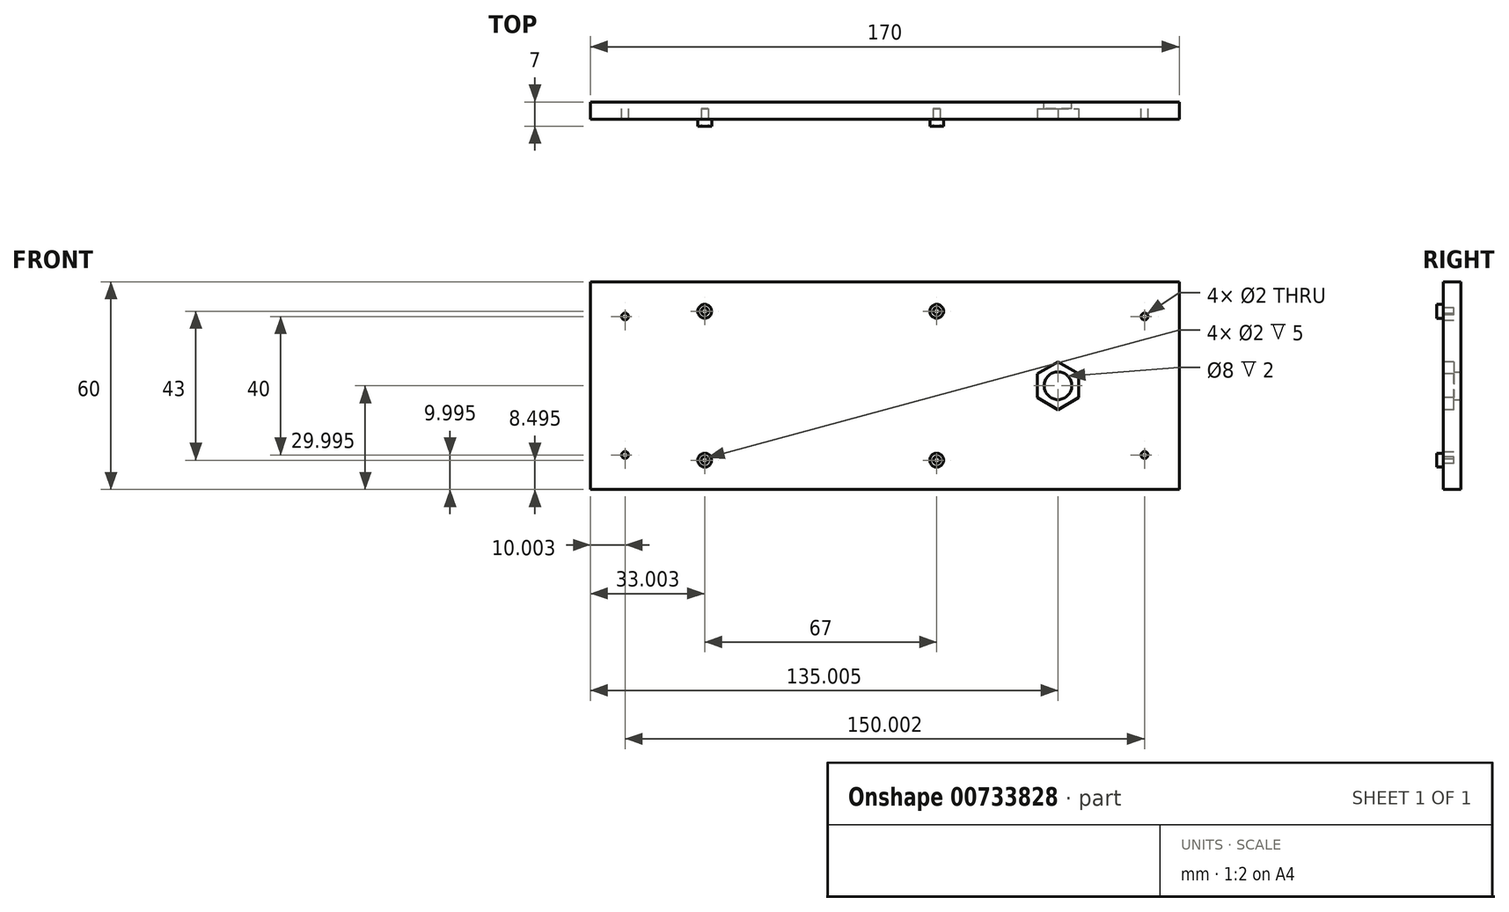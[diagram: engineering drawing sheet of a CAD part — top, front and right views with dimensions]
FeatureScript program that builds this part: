
annotation { "Feature Type Name" : "Feature", "Feature Type Description" : "" }
export const myFeature = defineFeature(function(context is Context, id is Id, definition is map)
    precondition{}
    {
        {
            var Q0;
            Q0=qCreatedBy(makeId("Front.planeOp"),FACE);
            var sketch = newSketch(context, id + "F0", { "sketchPlane" : qUnion([Q0])});
            skLineSegment(sketch, "E0.1", {"start": v(-75.65, -37.91) * mm, "end": v(-75.65, 22.09) * mm});
            skCircle(sketch, "E1", {"center": v(-65.65, -27.91) * mm, "radius": 1 * mm});
            skCircle(sketch, "E2", {"center": v(-65.65, 12.09) * mm, "radius": 1 * mm});
            skLineSegment(sketch, "E3.MirrorCS", {"start": v(94.35, 22.09) * mm, "end": v(-75.65, 22.09) * mm});
            skLineSegment(sketch, "E4.MirrorCS", {"start": v(94.35, -37.91) * mm, "end": v(94.35, 22.09) * mm});
            skCircle(sketch, "E5.MirrorC", {"center": v(84.35, 12.09) * mm, "radius": 1 * mm});
            skCircle(sketch, "E6.MirrorC", {"center": v(84.35, -27.91) * mm, "radius": 1 * mm});
            skLineSegment(sketch, "E7", {"start": v(-75.65, -37.91) * mm, "end": v(94.35, -37.91) * mm});
            skLineSegment(sketch, "E8", {"start": v(-75.65, 22.09) * mm, "end": v(-75.65, -7.91) * mm});
            skLineSegment(sketch, "E9", {"start": v(94.35, 22.09) * mm, "end": v(59.35, 22.09) * mm});
            skCircle(sketch, "E10", {"center": v(59.35, -7.91) * mm, "radius": 4 * mm});
            skLineSegment(sketch, "E11", {"start": v(-75.65, 22.09) * mm, "end": v(24.35, 22.09) * mm});
            skCircle(sketch, "E12", {"center": v(-42.65, -29.41) * mm, "radius": 2 * mm});
            skCircle(sketch, "E13", {"center": v(24.35, -29.41) * mm, "radius": 2 * mm});
            skCircle(sketch, "E14", {"center": v(24.35, 13.59) * mm, "radius": 2 * mm});
            skCircle(sketch, "E15", {"center": v(-42.65, 13.59) * mm, "radius": 2 * mm});
            skCircle(sketch, "E16", {"center": v(-42.65, 13.59) * mm, "radius": 1 * mm});
            skCircle(sketch, "E17", {"center": v(24.35, 13.59) * mm, "radius": 1 * mm});
            skCircle(sketch, "E18", {"center": v(24.35, -29.41) * mm, "radius": 1 * mm});
            skCircle(sketch, "E19", {"center": v(-42.65, -29.41) * mm, "radius": 1 * mm});
            skLineSegment(sketch, "E20.0", {"start": v(65.35, -4.45) * mm, "end": v(65.35, -11.38) * mm});
            skLineSegment(sketch, "E20.1", {"start": v(65.35, -11.38) * mm, "end": v(59.35, -14.84) * mm});
            skLineSegment(sketch, "E20.2", {"start": v(59.35, -14.84) * mm, "end": v(53.35, -11.38) * mm});
            skLineSegment(sketch, "E20.3", {"start": v(53.35, -11.38) * mm, "end": v(53.35, -4.45) * mm});
            skLineSegment(sketch, "E20.4", {"start": v(53.35, -4.45) * mm, "end": v(59.35, -0.99) * mm});
            skLineSegment(sketch, "E20.5", {"start": v(59.35, -0.99) * mm, "end": v(65.35, -4.45) * mm});
            skPoint(sketch, "E20.0.midPoint", {"position": v(65.35, -7.91) * mm});
            skSolve(sketch);
        }
        {
            var Q0;
            Q0=makeQuery(id+"F0.imprint","IMPRINT",FACE,{"disambiguationData":[TD([[makeQuery(id+"F0.imprint","IMPRINT",EDGE,{"derivedFrom":sQuery(id+"F0.wireOp",EDGE,"E18")}),1.0]])]});
            var Q1;
            Q1=makeQuery(id+"F0.imprint","IMPRINT",FACE,{"disambiguationData":[TD([[makeQuery(id+"F0.imprint","IMPRINT",EDGE,{"derivedFrom":sQuery(id+"F0.wireOp",EDGE,"E13")}),1.0]])]});
            var Q2;
            Q2=makeQuery(id+"F0.imprint","IMPRINT",FACE,{"disambiguationData":[TD([[makeQuery(id+"F0.imprint","IMPRINT",EDGE,{"derivedFrom":sQuery(id+"F0.wireOp",EDGE,"E0.1")}),-1.0]])]});
            var Q3;
            Q3=makeQuery(id+"F0.imprint","IMPRINT",FACE,{"disambiguationData":[TD([[makeQuery(id+"F0.imprint","IMPRINT",EDGE,{"derivedFrom":sQuery(id+"F0.wireOp",EDGE,"E12")}),1.0]])]});
            var Q4;
            Q4=makeQuery(id+"F0.imprint","IMPRINT",FACE,{"disambiguationData":[TD([[makeQuery(id+"F0.imprint","IMPRINT",EDGE,{"derivedFrom":sQuery(id+"F0.wireOp",EDGE,"E19")}),1.0]])]});
            var Q5;
            Q5=makeQuery(id+"F0.imprint","IMPRINT",FACE,{"disambiguationData":[TD([[makeQuery(id+"F0.imprint","IMPRINT",EDGE,{"derivedFrom":sQuery(id+"F0.wireOp",EDGE,"E15")}),1.0]])]});
            var Q6;
            Q6=makeQuery(id+"F0.imprint","IMPRINT",FACE,{"disambiguationData":[TD([[makeQuery(id+"F0.imprint","IMPRINT",EDGE,{"derivedFrom":sQuery(id+"F0.wireOp",EDGE,"E16")}),1.0]])]});
            var Q7;
            Q7=makeQuery(id+"F0.imprint","IMPRINT",FACE,{"disambiguationData":[TD([[makeQuery(id+"F0.imprint","IMPRINT",EDGE,{"derivedFrom":sQuery(id+"F0.wireOp",EDGE,"E14")}),1.0]])]});
            var Q8;
            Q8=makeQuery(id+"F0.imprint","IMPRINT",FACE,{"disambiguationData":[TD([[makeQuery(id+"F0.imprint","IMPRINT",EDGE,{"derivedFrom":sQuery(id+"F0.wireOp",EDGE,"E17")}),1.0]])]});
            var Q9;
            Q9=makeQuery(id+"F0.imprint","IMPRINT",FACE,{"disambiguationData":[TD([[makeQuery(id+"F0.imprint","IMPRINT",EDGE,{"derivedFrom":sQuery(id+"F0.wireOp",EDGE,"E10")}),-1.0]])]});
            extrude(context, id + "F1", {"entities" : qUnion([Q0, Q1, Q2, Q3, Q4, Q5, Q6, Q7, Q8, Q9]), "depth" : 5 * mm, "offsetDistance" : 25.4 * mm});
        }
        {
            var Q0;
            Q0=makeQuery(id+"F0.imprint","IMPRINT",FACE,{"disambiguationData":[TD([[makeQuery(id+"F0.imprint","IMPRINT",EDGE,{"derivedFrom":sQuery(id+"F0.wireOp",EDGE,"E19")}),1.0]])]});
            var Q1;
            Q1=makeQuery(id+"F0.imprint","IMPRINT",FACE,{"disambiguationData":[TD([[makeQuery(id+"F0.imprint","IMPRINT",EDGE,{"derivedFrom":sQuery(id+"F0.wireOp",EDGE,"E16")}),1.0]])]});
            var Q2;
            Q2=makeQuery(id+"F0.imprint","IMPRINT",FACE,{"disambiguationData":[TD([[makeQuery(id+"F0.imprint","IMPRINT",EDGE,{"derivedFrom":sQuery(id+"F0.wireOp",EDGE,"E17")}),1.0]])]});
            var Q3;
            Q3=makeQuery(id+"F0.imprint","IMPRINT",FACE,{"disambiguationData":[TD([[makeQuery(id+"F0.imprint","IMPRINT",EDGE,{"derivedFrom":sQuery(id+"F0.wireOp",EDGE,"E18")}),1.0]])]});
            var Q4;
            Q4=makeQuery(id+"F0.imprint","IMPRINT",FACE,{"disambiguationData":[TD([[makeQuery(id+"F0.imprint","IMPRINT",EDGE,{"derivedFrom":sQuery(id+"F0.wireOp",EDGE,"E15")}),1.0]])]});
            var Q5;
            Q5=makeQuery(id+"F0.imprint","IMPRINT",FACE,{"disambiguationData":[TD([[makeQuery(id+"F0.imprint","IMPRINT",EDGE,{"derivedFrom":sQuery(id+"F0.wireOp",EDGE,"E12")}),1.0]])]});
            var Q6;
            Q6=makeQuery(id+"F0.imprint","IMPRINT",FACE,{"disambiguationData":[TD([[makeQuery(id+"F0.imprint","IMPRINT",EDGE,{"derivedFrom":sQuery(id+"F0.wireOp",EDGE,"E13")}),1.0]])]});
            var Q7;
            Q7=makeQuery(id+"F0.imprint","IMPRINT",FACE,{"disambiguationData":[TD([[makeQuery(id+"F0.imprint","IMPRINT",EDGE,{"derivedFrom":sQuery(id+"F0.wireOp",EDGE,"E14")}),1.0]])]});
            extrude(context, id + "F2", {"entities" : qUnion([Q0, Q1, Q2, Q3, Q4, Q5, Q6, Q7]), "operationType" : NewBodyOperationType.ADD, "depth" : 7 * mm, "offsetDistance" : 25.4 * mm});
        }
        {
            var Q0;
            Q0=makeQuery(id+"F0.imprint","IMPRINT",FACE,{"disambiguationData":[TD([[makeQuery(id+"F0.imprint","IMPRINT",EDGE,{"derivedFrom":sQuery(id+"F0.wireOp",EDGE,"E16")}),1.0]])]});
            var Q1;
            Q1=makeQuery(id+"F0.imprint","IMPRINT",FACE,{"disambiguationData":[TD([[makeQuery(id+"F0.imprint","IMPRINT",EDGE,{"derivedFrom":sQuery(id+"F0.wireOp",EDGE,"E17")}),1.0]])]});
            var Q2;
            Q2=makeQuery(id+"F0.imprint","IMPRINT",FACE,{"disambiguationData":[TD([[makeQuery(id+"F0.imprint","IMPRINT",EDGE,{"derivedFrom":sQuery(id+"F0.wireOp",EDGE,"E19")}),1.0]])]});
            extrude(context, id + "F3", {"entities" : qUnion([Q0, Q1, Q2]), "operationType" : NewBodyOperationType.ADD, "depth" : 6.6 * mm, "offsetDistance" : 25.4 * mm});
        }
        {
            var Q0;
            Q0=makeQuery(id+"F2.opExtrude","CAP_FACE",FACE,{"disambiguationData":[OSD([sQuery(id+"F0.wireOp",EDGE,"E15")])],"isStart":false});
            var sketch = newSketch(context, id + "F4", { "sketchPlane" : qUnion([Q0])});
            skCircle(sketch, "E21", {"center": v(-42.65, 13.59) * mm, "radius": 1 * mm});
            skSolve(sketch);
        }
        {
            var Q0;
            Q0=makeQuery(id+"F4.imprint","IMPRINT",FACE,{"disambiguationData":[TD([[makeQuery(id+"F4.imprint","IMPRINT",EDGE,{"derivedFrom":sQuery(id+"F4.wireOp",EDGE,"E21")}),1.0]])]});
            extrude(context, id + "F5", {"entities" : qUnion([Q0]), "operationType" : NewBodyOperationType.REMOVE, "oppositeDirection" : true, "depth" : 5 * mm, "offsetDistance" : 25.4 * mm});
        }
        {
            var Q0;
            Q0=makeQuery(id+"F2.opExtrude","CAP_FACE",FACE,{"disambiguationData":[OSD([sQuery(id+"F0.wireOp",EDGE,"E14")])],"isStart":false});
            var sketch = newSketch(context, id + "F6", { "sketchPlane" : qUnion([Q0])});
            skCircle(sketch, "E22", {"center": v(24.35, 13.59) * mm, "radius": 1 * mm});
            skSolve(sketch);
        }
        {
            var Q0;
            Q0=makeQuery(id+"F6.imprint","IMPRINT",FACE,{"disambiguationData":[TD([[makeQuery(id+"F6.imprint","IMPRINT",EDGE,{"derivedFrom":sQuery(id+"F6.wireOp",EDGE,"E22")}),1.0]])]});
            extrude(context, id + "F7", {"entities" : qUnion([Q0]), "operationType" : NewBodyOperationType.REMOVE, "oppositeDirection" : true, "depth" : 5 * mm, "offsetDistance" : 25.4 * mm});
        }
        {
            var Q0;
            Q0=makeQuery(id+"F2.opExtrude","CAP_FACE",FACE,{"disambiguationData":[OSD([sQuery(id+"F0.wireOp",EDGE,"E12")])],"isStart":false});
            var sketch = newSketch(context, id + "F8", { "sketchPlane" : qUnion([Q0])});
            skCircle(sketch, "E23", {"center": v(-42.65, -29.41) * mm, "radius": 1 * mm});
            skSolve(sketch);
        }
        {
            var Q0;
            Q0=makeQuery(id+"F8.imprint","IMPRINT",FACE,{"disambiguationData":[TD([[makeQuery(id+"F8.imprint","IMPRINT",EDGE,{"derivedFrom":sQuery(id+"F8.wireOp",EDGE,"E23")}),1.0]])]});
            extrude(context, id + "F9", {"entities" : qUnion([Q0]), "operationType" : NewBodyOperationType.REMOVE, "oppositeDirection" : true, "depth" : 5 * mm, "offsetDistance" : 25.4 * mm});
        }
        {
            var Q0;
            Q0=makeQuery(id+"F2.opExtrude","CAP_FACE",FACE,{"disambiguationData":[OSD([sQuery(id+"F0.wireOp",EDGE,"E13")])],"isStart":false});
            var sketch = newSketch(context, id + "F10", { "sketchPlane" : qUnion([Q0])});
            skCircle(sketch, "E24", {"center": v(24.35, -29.41) * mm, "radius": 1 * mm});
            skSolve(sketch);
        }
        {
            var Q0;
            Q0=makeQuery(id+"F10.imprint","IMPRINT",FACE,{"disambiguationData":[TD([[makeQuery(id+"F10.imprint","IMPRINT",EDGE,{"derivedFrom":sQuery(id+"F10.wireOp",EDGE,"E24")}),1.0]])]});
            extrude(context, id + "F11", {"entities" : qUnion([Q0]), "operationType" : NewBodyOperationType.REMOVE, "oppositeDirection" : true, "depth" : 5 * mm, "offsetDistance" : 25.4 * mm});
        }
        {
            var Q0;
            Q0=makeQuery(id+"F1.opExtrude","CAP_FACE",FACE,{"disambiguationData":[OSD([sQuery(id+"F0.wireOp",EDGE,"E0.1"),sQuery(id+"F0.wireOp",EDGE,"E1"),sQuery(id+"F0.wireOp",EDGE,"E2"),sQuery(id+"F0.wireOp",EDGE,"E3.MirrorCS"),sQuery(id+"F0.wireOp",EDGE,"E4.MirrorCS"),sQuery(id+"F0.wireOp",EDGE,"E5.MirrorC"),sQuery(id+"F0.wireOp",EDGE,"E6.MirrorC"),sQuery(id+"F0.wireOp",EDGE,"E7"),sQuery(id+"F0.wireOp",EDGE,"E8"),sQuery(id+"F0.wireOp",EDGE,"E9"),sQuery(id+"F0.wireOp",EDGE,"E10"),sQuery(id+"F0.wireOp",EDGE,"E11")])],"isStart":false});
            var sketch = newSketch(context, id + "F12", { "sketchPlane" : qUnion([Q0])});
            skLineSegment(sketch, "E25.0", {"start": v(65.35, -4.45) * mm, "end": v(65.35, -11.38) * mm});
            skLineSegment(sketch, "E25.1", {"start": v(65.35, -11.38) * mm, "end": v(59.35, -14.84) * mm});
            skLineSegment(sketch, "E25.2", {"start": v(59.35, -14.84) * mm, "end": v(53.35, -11.38) * mm});
            skLineSegment(sketch, "E25.3", {"start": v(53.35, -11.38) * mm, "end": v(53.35, -4.45) * mm});
            skLineSegment(sketch, "E25.4", {"start": v(53.35, -4.45) * mm, "end": v(59.35, -0.99) * mm});
            skLineSegment(sketch, "E25.5", {"start": v(59.35, -0.99) * mm, "end": v(65.35, -4.45) * mm});
            skPoint(sketch, "E25.0.midPoint", {"position": v(65.35, -7.91) * mm});
            skSolve(sketch);
        }
        {
            var Q0;
            Q0 = qSketchRegion(id + "F12", true);
            extrude(context, id + "F13", {"entities" : qUnion([Q0]), "operationType" : NewBodyOperationType.REMOVE, "oppositeDirection" : true, "depth" : 3 * mm, "offsetDistance" : 25.4 * mm});
        }
    });
